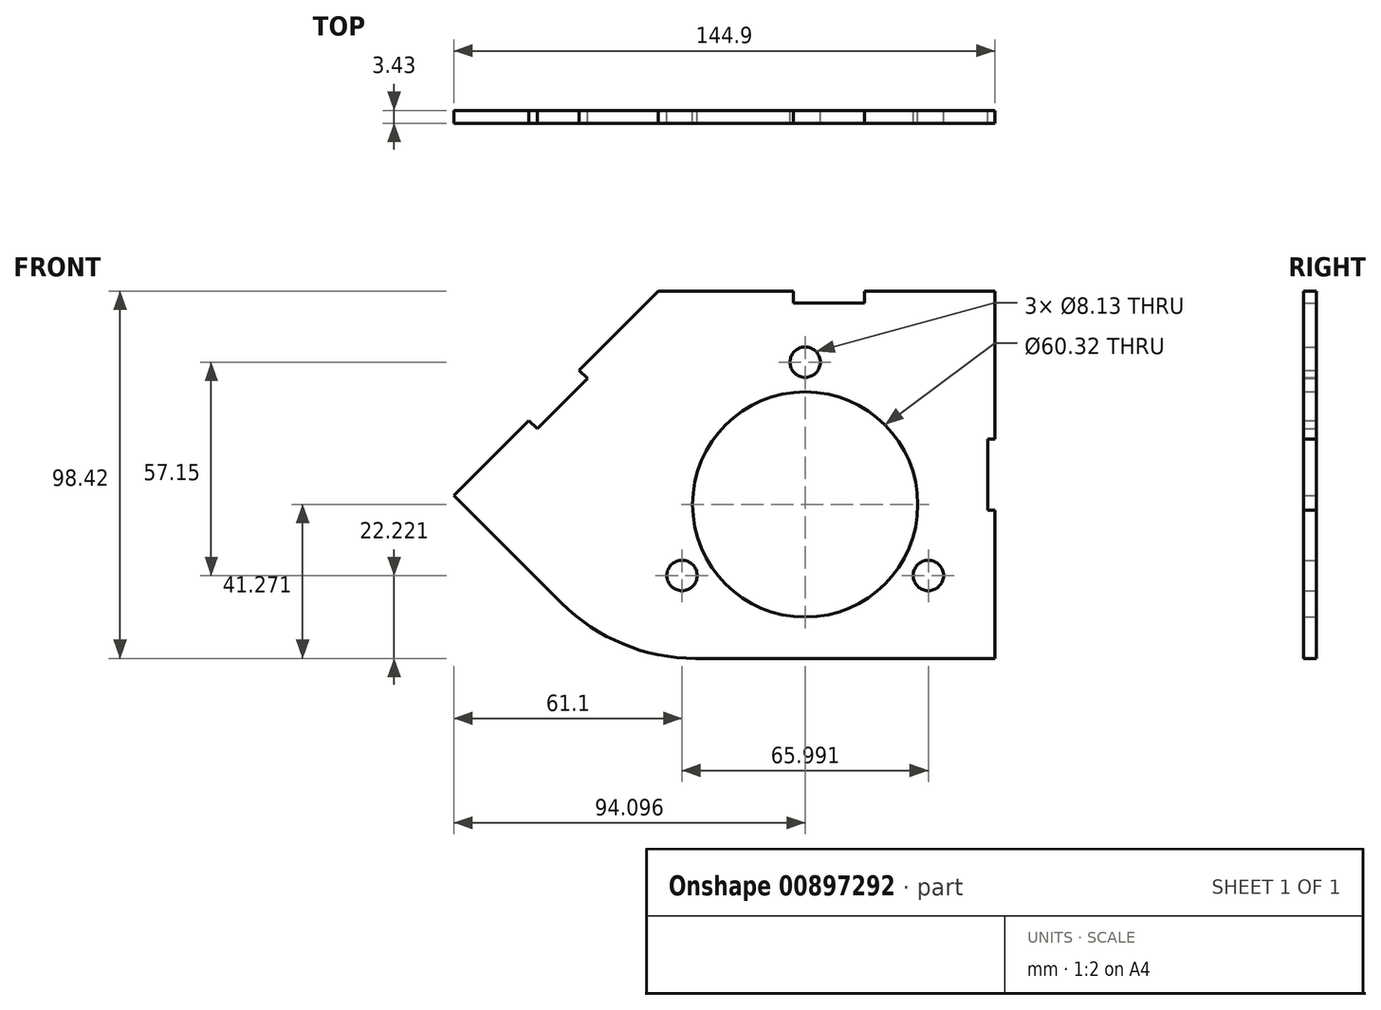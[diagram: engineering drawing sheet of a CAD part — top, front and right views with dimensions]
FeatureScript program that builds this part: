
annotation { "Feature Type Name" : "Feature", "Feature Type Description" : "" }
export const myFeature = defineFeature(function(context is Context, id is Id, definition is map)
    precondition{}
    {
        {
            var Q0;
            Q0=qCreatedBy(makeId("Front.planeOp"),FACE);
            var sketch = newSketch(context, id + "F0", { "sketchPlane" : qUnion([Q0])});
            skCircle(sketch, "E0", {"center": v(-347.27, 203.3) * mm, "radius": 30.16 * mm});
            skCircle(sketch, "E1", {"center": v(-347.27, 241.4) * mm, "radius": 4.06 * mm});
            skCircle(sketch, "E2", {"center": v(-314.28, 184.24) * mm, "radius": 4.06 * mm});
            skCircle(sketch, "E3", {"center": v(-380.27, 184.24) * mm, "radius": 4.06 * mm});
            skLineSegment(sketch, "E4", {"start": v(-419.06, 223.53) * mm, "end": v(-405.6, 237) * mm});
            skLineSegment(sketch, "E5", {"start": v(-405.6, 237) * mm, "end": v(-407.84, 239.25) * mm});
            skLineSegment(sketch, "E6", {"start": v(-350.45, 260.44) * mm, "end": v(-350.45, 257.27) * mm});
            skLineSegment(sketch, "E7", {"start": v(-350.45, 257.27) * mm, "end": v(-331.4, 257.27) * mm});
            skLineSegment(sketch, "E8", {"start": v(-331.4, 257.27) * mm, "end": v(-331.4, 260.44) * mm});
            skLineSegment(sketch, "E9", {"start": v(-296.47, 220.75) * mm, "end": v(-298.38, 220.75) * mm});
            skLineSegment(sketch, "E10", {"start": v(-298.38, 220.75) * mm, "end": v(-298.38, 201.7) * mm});
            skLineSegment(sketch, "E11", {"start": v(-298.38, 201.7) * mm, "end": v(-296.47, 201.7) * mm});
            skArc(sketch, "E12", {"start": v(-412.55, 176.9) * mm, "mid": v(-396.07, 165.88) * mm, "end": v(-376.63, 162.02) * mm});
            skLineSegment(sketch, "E13", {"start": v(-441.37, 205.72) * mm, "end": v(-412.55, 176.9) * mm});
            skLineSegment(sketch, "E14", {"start": v(-421.3, 225.78) * mm, "end": v(-419.06, 223.53) * mm});
            skLineSegment(sketch, "E15", {"start": v(-296.47, 220.75) * mm, "end": v(-296.47, 260.44) * mm});
            skLineSegment(sketch, "E16", {"start": v(-376.63, 162.02) * mm, "end": v(-296.47, 162.02) * mm});
            skLineSegment(sketch, "E17", {"start": v(-386.64, 260.44) * mm, "end": v(-407.84, 239.25) * mm});
            skLineSegment(sketch, "E18", {"start": v(-350.45, 260.44) * mm, "end": v(-386.64, 260.44) * mm});
            skLineSegment(sketch, "E19", {"start": v(-296.47, 260.44) * mm, "end": v(-331.4, 260.44) * mm});
            skLineSegment(sketch, "E20", {"start": v(-296.47, 162.02) * mm, "end": v(-296.47, 201.7) * mm});
            skLineSegment(sketch, "E21", {"start": v(-421.3, 225.78) * mm, "end": v(-441.37, 205.72) * mm});
            skSolve(sketch);
        }
        {
            var Q0;
            Q0 = qSketchRegion(id + "F0", true);
            extrude(context, id + "F1", {"entities" : qUnion([Q0]), "depth" : 3.43 * mm, "offsetDistance" : 25.4 * mm});
        }
    });
